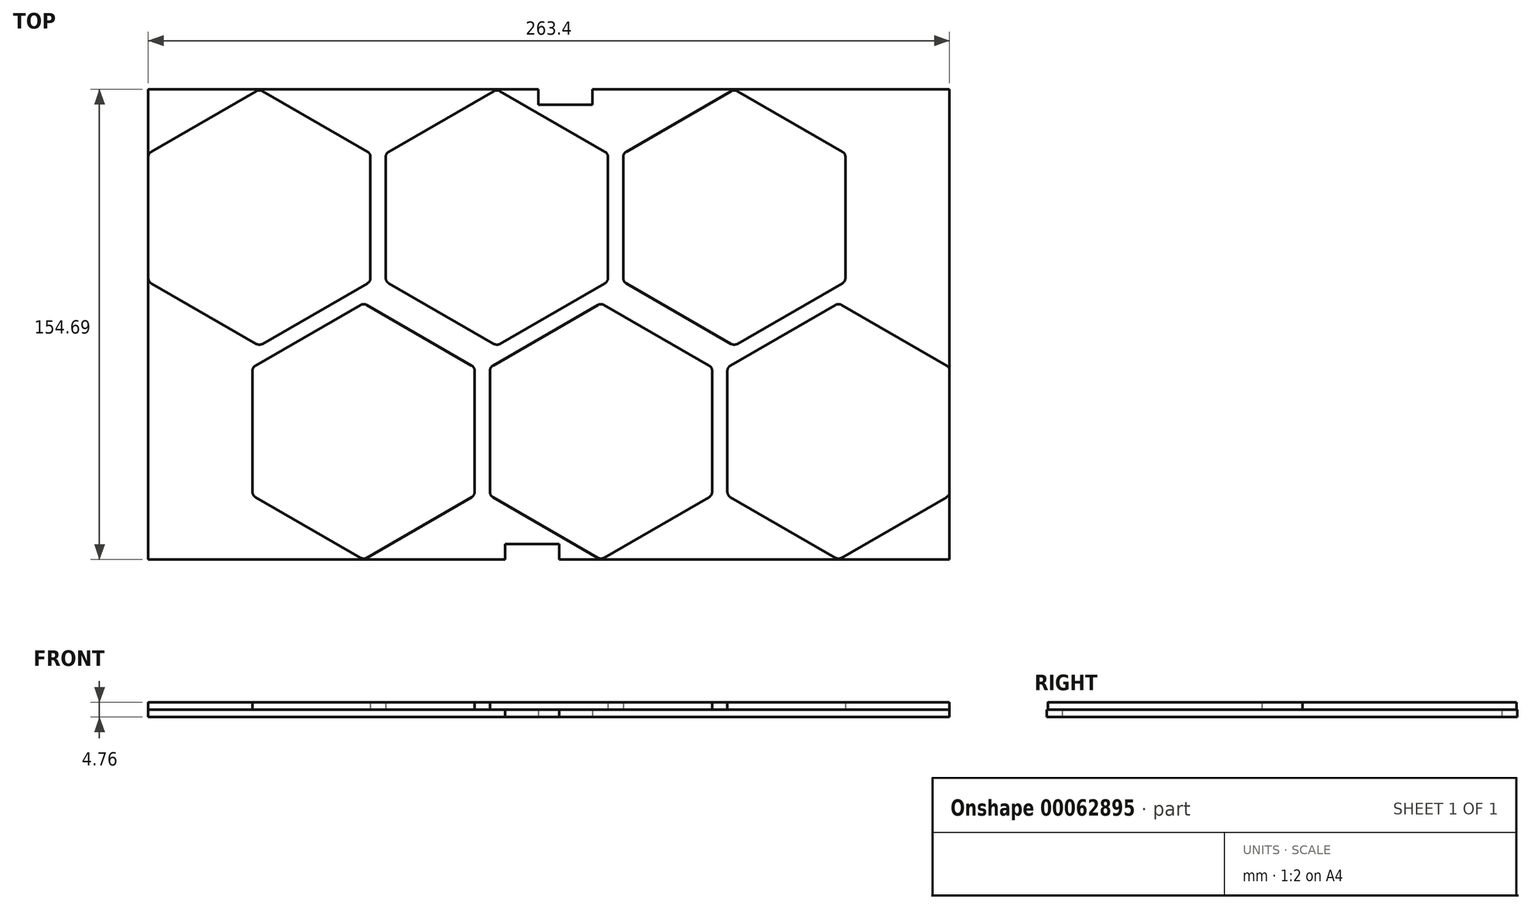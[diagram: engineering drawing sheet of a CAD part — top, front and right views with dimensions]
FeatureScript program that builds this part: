
annotation { "Feature Type Name" : "Feature", "Feature Type Description" : "" }
export const myFeature = defineFeature(function(context is Context, id is Id, definition is map)
    precondition{}
    {
        {
            var Q0;
            Q0=qCreatedBy(makeId("Top.planeOp"),FACE);
            var sketch = newSketch(context, id + "F0", { "sketchPlane" : qUnion([Q0])});
            skLineSegment(sketch, "E0.bottom", {"start": v(1.27, -155.96) * mm, "end": v(264.67, -155.96) * mm});
            skLineSegment(sketch, "E0.top", {"start": v(1.27, -1.27) * mm, "end": v(264.67, -1.27) * mm});
            skLineSegment(sketch, "E0.left", {"start": v(1.27, -155.96) * mm, "end": v(1.27, -1.27) * mm});
            skLineSegment(sketch, "E0.right", {"start": v(264.67, -155.96) * mm, "end": v(264.67, -1.27) * mm});
            skLineSegment(sketch, "E1.0", {"start": v(265.94, -157.23) * mm, "end": v(265.94, 0) * mm, "construction": true});
            skLineSegment(sketch, "E1.1", {"start": v(0, -157.23) * mm, "end": v(265.94, -157.23) * mm, "construction": true});
            skLineSegment(sketch, "E1.2", {"start": v(0, -157.23) * mm, "end": v(0, 0) * mm, "construction": true});
            skLineSegment(sketch, "E1.3", {"start": v(0, 0) * mm, "end": v(265.94, 0) * mm, "construction": true});
            skSolve(sketch);
        }
        {
            var Q0;
            Q0 = qSketchRegion(id + "F0", true);
            extrude(context, id + "F1", {"entities" : qUnion([Q0]), "depth" : 2.38 * mm});
        }
        {
            var Q0;
            Q0=makeQuery(id+"F1.opExtrude","CAP_FACE",FACE,{"disambiguationData":[OSD([sQuery(id+"F0.wireOp",EDGE,"E0.bottom"),sQuery(id+"F0.wireOp",EDGE,"E0.top"),sQuery(id+"F0.wireOp",EDGE,"E0.left"),sQuery(id+"F0.wireOp",EDGE,"E0.right")])],"isStart":false});
            var sketch = newSketch(context, id + "F2", { "sketchPlane" : qUnion([Q0])});
            skCircle(sketch, "E2.cCircle", {"center": v(37.78, -43.43) * mm, "radius": 36.51 * mm, "construction": true});
            skLineSegment(sketch, "E2.0", {"start": v(1.27, -22.35) * mm, "end": v(37.78, -1.27) * mm});
            skLineSegment(sketch, "E2.1", {"start": v(37.78, -1.27) * mm, "end": v(74.3, -22.35) * mm});
            skLineSegment(sketch, "E2.2", {"start": v(74.3, -22.35) * mm, "end": v(74.3, -64.51) * mm});
            skLineSegment(sketch, "E2.3", {"start": v(74.3, -64.51) * mm, "end": v(37.78, -85.6) * mm});
            skLineSegment(sketch, "E2.4", {"start": v(37.78, -85.6) * mm, "end": v(1.27, -64.51) * mm});
            skLineSegment(sketch, "E2.5", {"start": v(1.27, -64.51) * mm, "end": v(1.27, -22.35) * mm});
            skPoint(sketch, "E2.0.midPoint", {"position": v(19.53, -11.81) * mm});
            skCircle(sketch, "E3.cCircle", {"center": v(228.16, -113.8) * mm, "radius": 36.51 * mm, "construction": true});
            skLineSegment(sketch, "E3.0", {"start": v(191.64, -92.71) * mm, "end": v(228.16, -71.63) * mm});
            skLineSegment(sketch, "E3.1", {"start": v(228.16, -71.63) * mm, "end": v(264.67, -92.71) * mm});
            skLineSegment(sketch, "E3.2", {"start": v(264.67, -92.71) * mm, "end": v(264.67, -134.88) * mm});
            skLineSegment(sketch, "E3.3", {"start": v(264.67, -134.88) * mm, "end": v(228.16, -155.96) * mm});
            skLineSegment(sketch, "E3.4", {"start": v(228.16, -155.96) * mm, "end": v(191.64, -134.88) * mm});
            skLineSegment(sketch, "E3.5", {"start": v(191.64, -134.88) * mm, "end": v(191.64, -92.71) * mm});
            skPoint(sketch, "E3.0.midPoint", {"position": v(209.9, -82.17) * mm});
            skCircle(sketch, "E4.cCircle", {"center": v(150.1, -113.8) * mm, "radius": 36.51 * mm, "construction": true});
            skLineSegment(sketch, "E4.0", {"start": v(113.58, -92.71) * mm, "end": v(150.1, -71.63) * mm});
            skLineSegment(sketch, "E4.1", {"start": v(150.1, -71.63) * mm, "end": v(186.6, -92.71) * mm});
            skLineSegment(sketch, "E4.2", {"start": v(186.6, -92.71) * mm, "end": v(186.6, -134.88) * mm});
            skLineSegment(sketch, "E4.3", {"start": v(186.6, -134.88) * mm, "end": v(150.1, -155.96) * mm});
            skLineSegment(sketch, "E4.4", {"start": v(150.1, -155.96) * mm, "end": v(113.58, -134.88) * mm});
            skLineSegment(sketch, "E4.5", {"start": v(113.58, -134.88) * mm, "end": v(113.58, -92.71) * mm});
            skPoint(sketch, "E4.0.midPoint", {"position": v(131.84, -82.17) * mm});
            skCircle(sketch, "E5.cCircle", {"center": v(193.9, -43.43) * mm, "radius": 36.51 * mm, "construction": true});
            skLineSegment(sketch, "E5.0", {"start": v(157.4, -22.35) * mm, "end": v(193.9, -1.27) * mm});
            skLineSegment(sketch, "E5.1", {"start": v(193.9, -1.27) * mm, "end": v(230.42, -22.35) * mm});
            skLineSegment(sketch, "E5.2", {"start": v(230.42, -22.35) * mm, "end": v(230.42, -64.51) * mm});
            skLineSegment(sketch, "E5.3", {"start": v(230.42, -64.51) * mm, "end": v(193.9, -85.6) * mm});
            skLineSegment(sketch, "E5.4", {"start": v(193.9, -85.6) * mm, "end": v(157.4, -64.51) * mm});
            skLineSegment(sketch, "E5.5", {"start": v(157.4, -64.51) * mm, "end": v(157.4, -22.35) * mm});
            skPoint(sketch, "E5.0.midPoint", {"position": v(175.65, -11.81) * mm});
            skCircle(sketch, "E6.cCircle", {"center": v(72.03, -113.8) * mm, "radius": 36.51 * mm, "construction": true});
            skLineSegment(sketch, "E6.0", {"start": v(35.52, -92.71) * mm, "end": v(72.03, -71.63) * mm});
            skLineSegment(sketch, "E6.1", {"start": v(72.03, -71.63) * mm, "end": v(108.54, -92.71) * mm});
            skLineSegment(sketch, "E6.2", {"start": v(108.54, -92.71) * mm, "end": v(108.54, -134.88) * mm});
            skLineSegment(sketch, "E6.3", {"start": v(108.54, -134.88) * mm, "end": v(72.03, -155.96) * mm});
            skLineSegment(sketch, "E6.4", {"start": v(72.03, -155.96) * mm, "end": v(35.52, -134.88) * mm});
            skLineSegment(sketch, "E6.5", {"start": v(35.52, -134.88) * mm, "end": v(35.52, -92.71) * mm});
            skPoint(sketch, "E6.0.midPoint", {"position": v(53.78, -82.17) * mm});
            skCircle(sketch, "E7.cCircle", {"center": v(115.84, -43.43) * mm, "radius": 36.51 * mm, "construction": true});
            skLineSegment(sketch, "E7.0", {"start": v(79.33, -22.35) * mm, "end": v(115.84, -1.27) * mm});
            skLineSegment(sketch, "E7.1", {"start": v(115.84, -1.27) * mm, "end": v(152.36, -22.35) * mm});
            skLineSegment(sketch, "E7.2", {"start": v(152.36, -22.35) * mm, "end": v(152.36, -64.51) * mm});
            skLineSegment(sketch, "E7.3", {"start": v(152.36, -64.51) * mm, "end": v(115.84, -85.6) * mm});
            skLineSegment(sketch, "E7.4", {"start": v(115.84, -85.6) * mm, "end": v(79.33, -64.51) * mm});
            skLineSegment(sketch, "E7.5", {"start": v(79.33, -64.51) * mm, "end": v(79.33, -22.35) * mm});
            skPoint(sketch, "E7.0.midPoint", {"position": v(97.59, -11.81) * mm});
            skLineSegment(sketch, "E8.bottom", {"start": v(118.62, -155.96) * mm, "end": v(136.4, -155.96) * mm});
            skLineSegment(sketch, "E8.top", {"start": v(118.62, -150.88) * mm, "end": v(136.4, -150.88) * mm});
            skLineSegment(sketch, "E8.left", {"start": v(118.62, -155.96) * mm, "end": v(118.62, -150.88) * mm});
            skLineSegment(sketch, "E8.right", {"start": v(136.4, -155.96) * mm, "end": v(136.4, -150.88) * mm});
            skLineSegment(sketch, "E9.bottom", {"start": v(129.54, -1.27) * mm, "end": v(147.32, -1.27) * mm});
            skLineSegment(sketch, "E9.top", {"start": v(129.54, -6.35) * mm, "end": v(147.32, -6.35) * mm});
            skLineSegment(sketch, "E9.left", {"start": v(129.54, -1.27) * mm, "end": v(129.54, -6.35) * mm});
            skLineSegment(sketch, "E9.right", {"start": v(147.32, -1.27) * mm, "end": v(147.32, -6.35) * mm});
            skLineSegment(sketch, "E10", {"start": v(72.03, -71.63) * mm, "end": v(69.51, -67.27) * mm, "construction": true});
            skLineSegment(sketch, "E11", {"start": v(150.1, -71.63) * mm, "end": v(147.58, -67.27) * mm, "construction": true});
            skLineSegment(sketch, "E12", {"start": v(228.16, -71.63) * mm, "end": v(225.64, -67.27) * mm, "construction": true});
            skLineSegment(sketch, "E13", {"start": v(157.4, -58.61) * mm, "end": v(152.36, -58.61) * mm, "construction": true});
            skLineSegment(sketch, "E14", {"start": v(79.33, -59.8) * mm, "end": v(74.3, -59.8) * mm, "construction": true});
            skLineSegment(sketch, "E15", {"start": v(108.54, -98.86) * mm, "end": v(113.58, -98.86) * mm, "construction": true});
            skLineSegment(sketch, "E16", {"start": v(186.6, -97.96) * mm, "end": v(191.64, -97.96) * mm, "construction": true});
            skSolve(sketch);
        }
        {
            var Q0;
            Q0 = qSketchRegion(id + "F2", true);
            extrude(context, id + "F3", {"entities" : qUnion([Q0]), "depth" : 2.38 * mm});
        }
        {
            var Q0;
            Q0=makeQuery(id+"F3.opExtrude","SWEPT_EDGE",EDGE,{"disambiguationData":[OSD([sQuery(id+"F2.wireOp",EDGE,"E2.3"),sQuery(id+"F2.wireOp",EDGE,"E2.4")])]});
            var Q1;
            Q1=makeQuery(id+"F3.opExtrude","SWEPT_EDGE",EDGE,{"disambiguationData":[OSD([sQuery(id+"F0.wireOp",EDGE,"E0.left"),sQuery(id+"F2.wireOp",EDGE,"E2.4"),sQuery(id+"F2.wireOp",EDGE,"E2.5")])]});
            var Q2;
            Q2=makeQuery(id+"F3.opExtrude","SWEPT_EDGE",EDGE,{"disambiguationData":[OSD([sQuery(id+"F2.wireOp",EDGE,"E6.4"),sQuery(id+"F2.wireOp",EDGE,"E6.5")])]});
            var Q3;
            Q3=makeQuery(id+"F3.opExtrude","SWEPT_EDGE",EDGE,{"disambiguationData":[OSD([sQuery(id+"F0.wireOp",EDGE,"E0.bottom"),sQuery(id+"F2.wireOp",EDGE,"E6.3"),sQuery(id+"F2.wireOp",EDGE,"E6.4")])]});
            var Q4;
            Q4=makeQuery(id+"F3.opExtrude","SWEPT_EDGE",EDGE,{"disambiguationData":[OSD([sQuery(id+"F2.wireOp",EDGE,"E6.2"),sQuery(id+"F2.wireOp",EDGE,"E6.3")])]});
            var Q5;
            Q5=makeQuery(id+"F3.opExtrude","SWEPT_EDGE",EDGE,{"disambiguationData":[OSD([sQuery(id+"F2.wireOp",EDGE,"E4.4"),sQuery(id+"F2.wireOp",EDGE,"E4.5")])]});
            var Q6;
            Q6=makeQuery(id+"F3.opExtrude","SWEPT_EDGE",EDGE,{"disambiguationData":[OSD([sQuery(id+"F0.wireOp",EDGE,"E0.bottom"),sQuery(id+"F2.wireOp",EDGE,"E4.3"),sQuery(id+"F2.wireOp",EDGE,"E4.4")])]});
            var Q7;
            Q7=makeQuery(id+"F3.opExtrude","SWEPT_EDGE",EDGE,{"disambiguationData":[OSD([sQuery(id+"F2.wireOp",EDGE,"E7.2"),sQuery(id+"F2.wireOp",EDGE,"E7.3")])]});
            var Q8;
            Q8=makeQuery(id+"F3.opExtrude","SWEPT_EDGE",EDGE,{"disambiguationData":[OSD([sQuery(id+"F2.wireOp",EDGE,"E5.4"),sQuery(id+"F2.wireOp",EDGE,"E5.5")])]});
            var Q9;
            Q9=makeQuery(id+"F3.opExtrude","SWEPT_EDGE",EDGE,{"disambiguationData":[OSD([sQuery(id+"F2.wireOp",EDGE,"E4.2"),sQuery(id+"F2.wireOp",EDGE,"E4.3")])]});
            var Q10;
            Q10=makeQuery(id+"F3.opExtrude","SWEPT_EDGE",EDGE,{"disambiguationData":[OSD([sQuery(id+"F2.wireOp",EDGE,"E5.3"),sQuery(id+"F2.wireOp",EDGE,"E5.4")])]});
            var Q11;
            Q11=makeQuery(id+"F3.opExtrude","SWEPT_EDGE",EDGE,{"disambiguationData":[OSD([sQuery(id+"F2.wireOp",EDGE,"E3.4"),sQuery(id+"F2.wireOp",EDGE,"E3.5")])]});
            var Q12;
            Q12=makeQuery(id+"F3.opExtrude","SWEPT_EDGE",EDGE,{"disambiguationData":[OSD([sQuery(id+"F0.wireOp",EDGE,"E0.bottom"),sQuery(id+"F2.wireOp",EDGE,"E3.3"),sQuery(id+"F2.wireOp",EDGE,"E3.4")])]});
            var Q13;
            Q13=makeQuery(id+"F3.opExtrude","SWEPT_EDGE",EDGE,{"disambiguationData":[OSD([sQuery(id+"F2.wireOp",EDGE,"E5.2"),sQuery(id+"F2.wireOp",EDGE,"E5.3")])]});
            var Q14;
            Q14=makeQuery(id+"F3.opExtrude","SWEPT_EDGE",EDGE,{"disambiguationData":[OSD([sQuery(id+"F0.wireOp",EDGE,"E0.right"),sQuery(id+"F2.wireOp",EDGE,"E3.2"),sQuery(id+"F2.wireOp",EDGE,"E3.3")])]});
            var Q15;
            Q15=makeQuery(id+"F3.opExtrude","SWEPT_EDGE",EDGE,{"disambiguationData":[OSD([sQuery(id+"F2.wireOp",EDGE,"E2.2"),sQuery(id+"F2.wireOp",EDGE,"E2.3")])]});
            var Q16;
            Q16=makeQuery(id+"F3.opExtrude","SWEPT_EDGE",EDGE,{"disambiguationData":[OSD([sQuery(id+"F2.wireOp",EDGE,"E7.4"),sQuery(id+"F2.wireOp",EDGE,"E7.5")])]});
            var Q17;
            Q17=makeQuery(id+"F3.opExtrude","SWEPT_EDGE",EDGE,{"disambiguationData":[OSD([sQuery(id+"F2.wireOp",EDGE,"E7.3"),sQuery(id+"F2.wireOp",EDGE,"E7.4")])]});
            var Q18;
            Q18=makeQuery(id+"F3.opExtrude","SWEPT_EDGE",EDGE,{"disambiguationData":[OSD([sQuery(id+"F2.wireOp",EDGE,"E6.0"),sQuery(id+"F2.wireOp",EDGE,"E6.5")])]});
            var Q19;
            Q19=makeQuery(id+"F3.opExtrude","SWEPT_EDGE",EDGE,{"disambiguationData":[OSD([sQuery(id+"F2.wireOp",EDGE,"E6.0"),sQuery(id+"F2.wireOp",EDGE,"E6.1")])]});
            var Q20;
            Q20=makeQuery(id+"F3.opExtrude","SWEPT_EDGE",EDGE,{"disambiguationData":[OSD([sQuery(id+"F0.wireOp",EDGE,"E0.top"),sQuery(id+"F2.wireOp",EDGE,"E2.0"),sQuery(id+"F2.wireOp",EDGE,"E2.1")])]});
            var Q21;
            Q21=makeQuery(id+"F3.opExtrude","SWEPT_EDGE",EDGE,{"disambiguationData":[OSD([sQuery(id+"F0.wireOp",EDGE,"E0.left"),sQuery(id+"F2.wireOp",EDGE,"E2.0"),sQuery(id+"F2.wireOp",EDGE,"E2.5")])]});
            var Q22;
            Q22=makeQuery(id+"F3.opExtrude","SWEPT_EDGE",EDGE,{"disambiguationData":[OSD([sQuery(id+"F2.wireOp",EDGE,"E2.1"),sQuery(id+"F2.wireOp",EDGE,"E2.2")])]});
            var Q23;
            Q23=makeQuery(id+"F3.opExtrude","SWEPT_EDGE",EDGE,{"disambiguationData":[OSD([sQuery(id+"F2.wireOp",EDGE,"E7.0"),sQuery(id+"F2.wireOp",EDGE,"E7.5")])]});
            var Q24;
            Q24=makeQuery(id+"F3.opExtrude","SWEPT_EDGE",EDGE,{"disambiguationData":[OSD([sQuery(id+"F2.wireOp",EDGE,"E4.0"),sQuery(id+"F2.wireOp",EDGE,"E4.5")])]});
            var Q25;
            Q25=makeQuery(id+"F3.opExtrude","SWEPT_EDGE",EDGE,{"disambiguationData":[OSD([sQuery(id+"F2.wireOp",EDGE,"E4.0"),sQuery(id+"F2.wireOp",EDGE,"E4.1")])]});
            var Q26;
            Q26=makeQuery(id+"F3.opExtrude","SWEPT_EDGE",EDGE,{"disambiguationData":[OSD([sQuery(id+"F0.wireOp",EDGE,"E0.top"),sQuery(id+"F2.wireOp",EDGE,"E7.0"),sQuery(id+"F2.wireOp",EDGE,"E7.1")])]});
            var Q27;
            Q27=makeQuery(id+"F3.opExtrude","SWEPT_EDGE",EDGE,{"disambiguationData":[OSD([sQuery(id+"F2.wireOp",EDGE,"E7.1"),sQuery(id+"F2.wireOp",EDGE,"E7.2")])]});
            var Q28;
            Q28=makeQuery(id+"F3.opExtrude","SWEPT_EDGE",EDGE,{"disambiguationData":[OSD([sQuery(id+"F2.wireOp",EDGE,"E5.0"),sQuery(id+"F2.wireOp",EDGE,"E5.5")])]});
            var Q29;
            Q29=makeQuery(id+"F3.opExtrude","SWEPT_EDGE",EDGE,{"disambiguationData":[OSD([sQuery(id+"F2.wireOp",EDGE,"E5.1"),sQuery(id+"F2.wireOp",EDGE,"E5.2")])]});
            var Q30;
            Q30=makeQuery(id+"F3.opExtrude","SWEPT_EDGE",EDGE,{"disambiguationData":[OSD([sQuery(id+"F0.wireOp",EDGE,"E0.top"),sQuery(id+"F2.wireOp",EDGE,"E5.0"),sQuery(id+"F2.wireOp",EDGE,"E5.1")])]});
            var Q31;
            Q31=makeQuery(id+"F3.opExtrude","SWEPT_EDGE",EDGE,{"disambiguationData":[OSD([sQuery(id+"F2.wireOp",EDGE,"E4.1"),sQuery(id+"F2.wireOp",EDGE,"E4.2")])]});
            var Q32;
            Q32=makeQuery(id+"F3.opExtrude","SWEPT_EDGE",EDGE,{"disambiguationData":[OSD([sQuery(id+"F2.wireOp",EDGE,"E3.0"),sQuery(id+"F2.wireOp",EDGE,"E3.5")])]});
            var Q33;
            Q33=makeQuery(id+"F3.opExtrude","SWEPT_EDGE",EDGE,{"disambiguationData":[OSD([sQuery(id+"F2.wireOp",EDGE,"E3.0"),sQuery(id+"F2.wireOp",EDGE,"E3.1")])]});
            var Q34;
            Q34=makeQuery(id+"F3.opExtrude","SWEPT_EDGE",EDGE,{"disambiguationData":[OSD([sQuery(id+"F0.wireOp",EDGE,"E0.right"),sQuery(id+"F2.wireOp",EDGE,"E3.1"),sQuery(id+"F2.wireOp",EDGE,"E3.2")])]});
            var Q35;
            Q35=makeQuery(id+"F3.opExtrude","SWEPT_EDGE",EDGE,{"disambiguationData":[OSD([sQuery(id+"F2.wireOp",EDGE,"E6.1"),sQuery(id+"F2.wireOp",EDGE,"E6.2")])]});
            fillet(context, id + "F4", {"entities" : qUnion([Q0, Q1, Q2, Q3, Q4, Q5, Q6, Q7, Q8, Q9, Q10, Q11, Q12, Q13, Q14, Q15, Q16, Q17, Q18, Q19, Q20, Q21, Q22, Q23, Q24, Q25, Q26, Q27, Q28, Q29, Q30, Q31, Q32, Q33, Q34, Q35]), "radius" : 2 * mm, "tangentPropagation" : true, "allowEdgeOverflow" : false});
        }
        {
            var Q0;
            Q0=makeQuery(id+"F0.imprint","IMPRINT",FACE,{"disambiguationData":[TD([[makeQuery(id+"F0.imprint","IMPRINT",EDGE,{"derivedFrom":sQuery(id+"F0.wireOp",EDGE,"E0.bottom")}),1.0]])]});
            var sketch = newSketch(context, id + "F5", { "sketchPlane" : qUnion([Q0])});
            skLineSegment(sketch, "E17.0", {"start": v(118.62, -150.88) * mm, "end": v(136.4, -150.88) * mm});
            skLineSegment(sketch, "E17.1", {"start": v(118.62, -155.96) * mm, "end": v(118.62, -150.88) * mm});
            skLineSegment(sketch, "E17.2", {"start": v(118.62, -155.96) * mm, "end": v(136.4, -155.96) * mm});
            skLineSegment(sketch, "E17.3", {"start": v(136.4, -155.96) * mm, "end": v(136.4, -150.88) * mm});
            skLineSegment(sketch, "E18.0", {"start": v(129.54, -6.35) * mm, "end": v(147.32, -6.35) * mm});
            skLineSegment(sketch, "E18.1", {"start": v(129.54, -1.27) * mm, "end": v(147.32, -1.27) * mm});
            skLineSegment(sketch, "E18.2", {"start": v(147.32, -1.27) * mm, "end": v(147.32, -6.35) * mm});
            skLineSegment(sketch, "E18.3", {"start": v(129.54, -1.27) * mm, "end": v(129.54, -6.35) * mm});
            skSolve(sketch);
        }
        {
            var Q0;
            Q0 = qSketchRegion(id + "F5", true);
            extrude(context, id + "F6", {"entities" : qUnion([Q0]), "operationType" : NewBodyOperationType.REMOVE, "endBound" : BoundingType.THROUGH_ALL, "depth" : 25.4 * mm});
        }
    });
